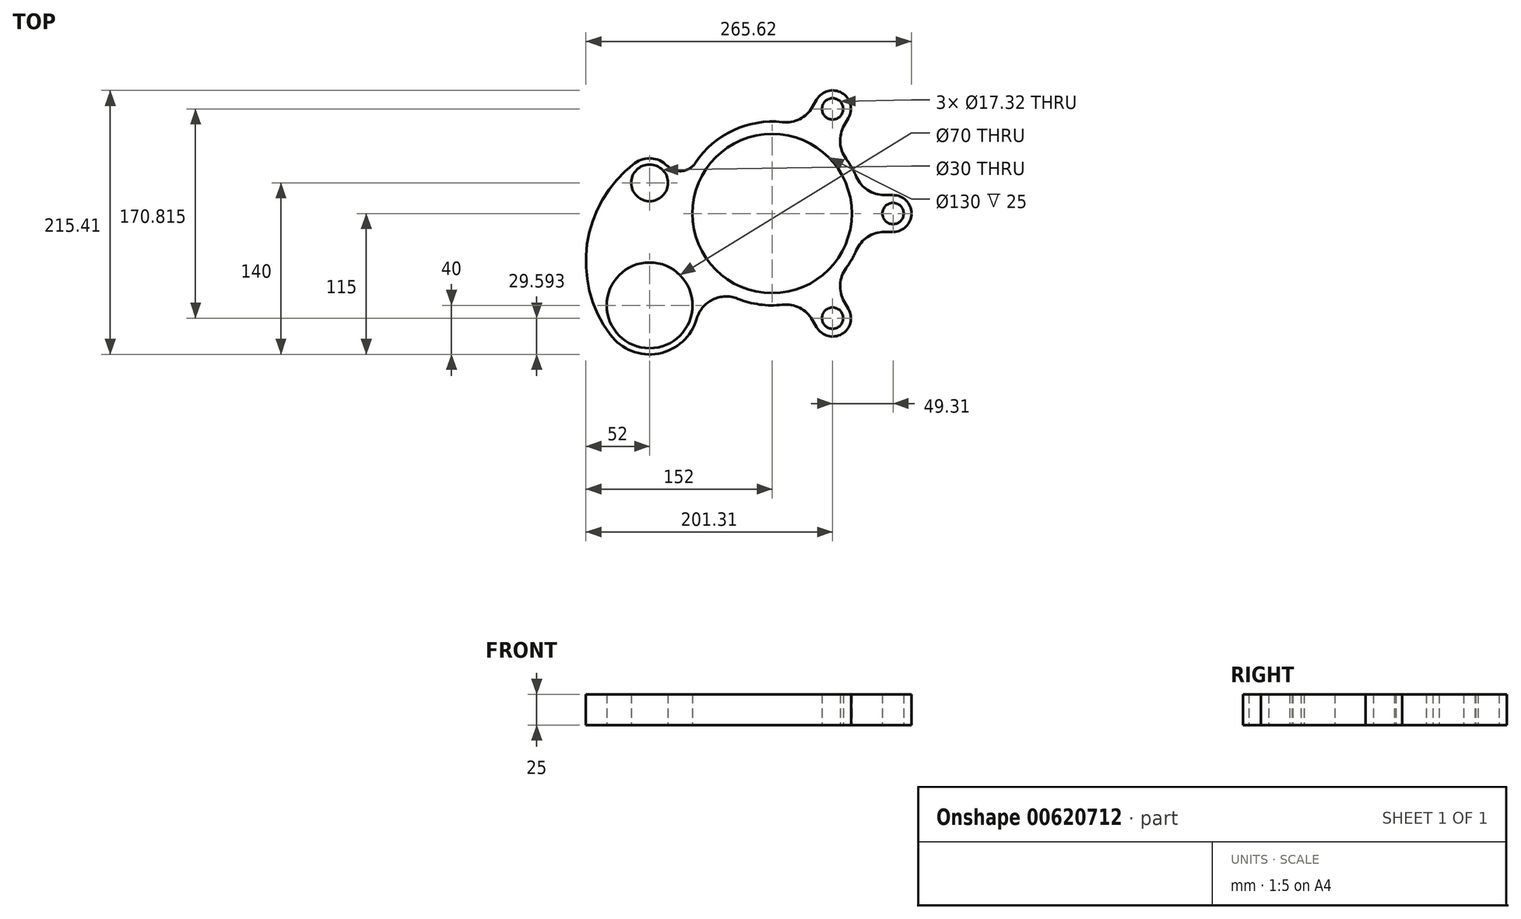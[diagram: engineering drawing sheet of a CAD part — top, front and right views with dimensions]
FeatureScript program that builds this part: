
annotation { "Feature Type Name" : "Feature", "Feature Type Description" : "" }
export const myFeature = defineFeature(function(context is Context, id is Id, definition is map)
    precondition{}
    {
        {
            var Q0;
            Q0=qCreatedBy(makeId("Top.planeOp"),FACE);
            var sketch = newSketch(context, id + "F0", { "sketchPlane" : qUnion([Q0])});
            skCircle(sketch, "E0", {"center": v(0, 0) * mm, "radius": 65 * mm});
            skCircle(sketch, "E1", {"center": v(0, 0) * mm, "radius": 75 * mm});
            skLineSegment(sketch, "E2", {"start": v(0, 0) * mm, "end": v(98.62, 0) * mm});
            skLineSegment(sketch, "E3", {"start": v(0, 0) * mm, "end": v(49.31, 85.4) * mm});
            skLineSegment(sketch, "E4", {"start": v(0, 0) * mm, "end": v(49.31, -85.4) * mm});
            skCircle(sketch, "E5", {"center": v(49.31, 85.4) * mm, "radius": 15 * mm});
            skCircle(sketch, "E6", {"center": v(98.62, 0) * mm, "radius": 15 * mm});
            skCircle(sketch, "E7", {"center": v(49.31, -85.4) * mm, "radius": 15 * mm});
            skCircle(sketch, "E8", {"center": v(49.31, 85.4) * mm, "radius": 8.66 * mm});
            skCircle(sketch, "E9", {"center": v(98.62, 0) * mm, "radius": 8.66 * mm});
            skCircle(sketch, "E10", {"center": v(49.31, -85.4) * mm, "radius": 8.66 * mm});
            skCircle(sketch, "E11", {"center": v(49.31, 85.4) * mm, "radius": 7.5 * mm});
            skCircle(sketch, "E12", {"center": v(98.62, 0) * mm, "radius": 7.5 * mm});
            skCircle(sketch, "E13", {"center": v(49.31, -85.4) * mm, "radius": 7.5 * mm});
            skLineSegment(sketch, "E14", {"start": v(73.48, 15) * mm, "end": v(98.62, 15) * mm});
            skLineSegment(sketch, "E15", {"start": v(73.48, -15) * mm, "end": v(98.62, -15) * mm});
            skLineSegment(sketch, "E16", {"start": v(49.31, 85.4) * mm, "end": v(62.3, 77.9) * mm});
            skLineSegment(sketch, "E17", {"start": v(49.31, 85.4) * mm, "end": v(36.32, 92.9) * mm});
            skLineSegment(sketch, "E18", {"start": v(62.3, 77.9) * mm, "end": v(49.73, 56.14) * mm});
            skLineSegment(sketch, "E19", {"start": v(36.32, 92.9) * mm, "end": v(23.75, 71.14) * mm});
            skLineSegment(sketch, "E20", {"start": v(49.31, -85.4) * mm, "end": v(62.3, -77.9) * mm});
            skLineSegment(sketch, "E21", {"start": v(49.31, -85.4) * mm, "end": v(36.32, -92.9) * mm});
            skLineSegment(sketch, "E22", {"start": v(36.32, -92.9) * mm, "end": v(23.75, -71.14) * mm});
            skLineSegment(sketch, "E23", {"start": v(62.3, -77.9) * mm, "end": v(49.73, -56.14) * mm});
            skCircle(sketch, "E24", {"center": v(-100, 25) * mm, "radius": 15 * mm});
            skLineSegment(sketch, "E25", {"start": v(0, 0) * mm, "end": v(-131.1, 0) * mm});
            skCircle(sketch, "E26", {"center": v(-100, -75) * mm, "radius": 35 * mm});
            skCircle(sketch, "E27", {"center": v(-100, -75) * mm, "radius": 40 * mm});
            skCircle(sketch, "E28", {"center": v(-100, 25) * mm, "radius": 20 * mm});
            skArc(sketch, "E29", {"start": v(-112, 41) * mm, "mid": v(-151, -24.86) * mm, "end": v(-132, -99) * mm});
            skArc(sketch, "E30", {"start": v(-28.1, -69.54) * mm, "mid": v(-48.46, -70.27) * mm, "end": v(-61.51, -85.9) * mm});
            skArc(sketch, "E31", {"start": v(-85.77, 39.06) * mm, "mid": v(-73.64, 34.67) * mm, "end": v(-62.58, 41.33) * mm});
            skSolve(sketch);
        }
        {
            var Q0;
            Q0 = qSketchRegion(id + "F0", true);
            extrude(context, id + "F1", {"entities" : qUnion([Q0]), "depth" : 25 * mm, "offsetDistance" : 25 * mm});
        }
        {
            var Q0;
            Q0=makeQuery(id+"F1.opExtrude","SWEPT_EDGE",EDGE,{"disambiguationData":[OSD([sQuery(id+"F0.wireOp",EDGE,"E1"),sQuery(id+"F0.wireOp",EDGE,"E23")])]});
            var Q1;
            Q1=makeQuery(id+"F1.opExtrude","SWEPT_EDGE",EDGE,{"disambiguationData":[OSD([sQuery(id+"F0.wireOp",EDGE,"E1"),sQuery(id+"F0.wireOp",EDGE,"E15")])]});
            var Q2;
            Q2=makeQuery(id+"F1.opExtrude","SWEPT_EDGE",EDGE,{"disambiguationData":[OSD([sQuery(id+"F0.wireOp",EDGE,"E1"),sQuery(id+"F0.wireOp",EDGE,"E22")])]});
            var Q3;
            Q3=makeQuery(id+"F1.opExtrude","SWEPT_EDGE",EDGE,{"disambiguationData":[OSD([sQuery(id+"F0.wireOp",EDGE,"E1"),sQuery(id+"F0.wireOp",EDGE,"E14")])]});
            var Q4;
            Q4=makeQuery(id+"F1.opExtrude","SWEPT_EDGE",EDGE,{"disambiguationData":[OSD([sQuery(id+"F0.wireOp",EDGE,"E1"),sQuery(id+"F0.wireOp",EDGE,"E18")])]});
            var Q5;
            Q5=makeQuery(id+"F1.opExtrude","SWEPT_EDGE",EDGE,{"disambiguationData":[OSD([sQuery(id+"F0.wireOp",EDGE,"E1"),sQuery(id+"F0.wireOp",EDGE,"E19")])]});
            fillet(context, id + "F2", {"entities" : qUnion([Q0, Q1, Q2, Q3, Q4, Q5]), "radius" : 25 * mm, "tangentPropagation" : true, "allowEdgeOverflow" : false});
        }
    });
